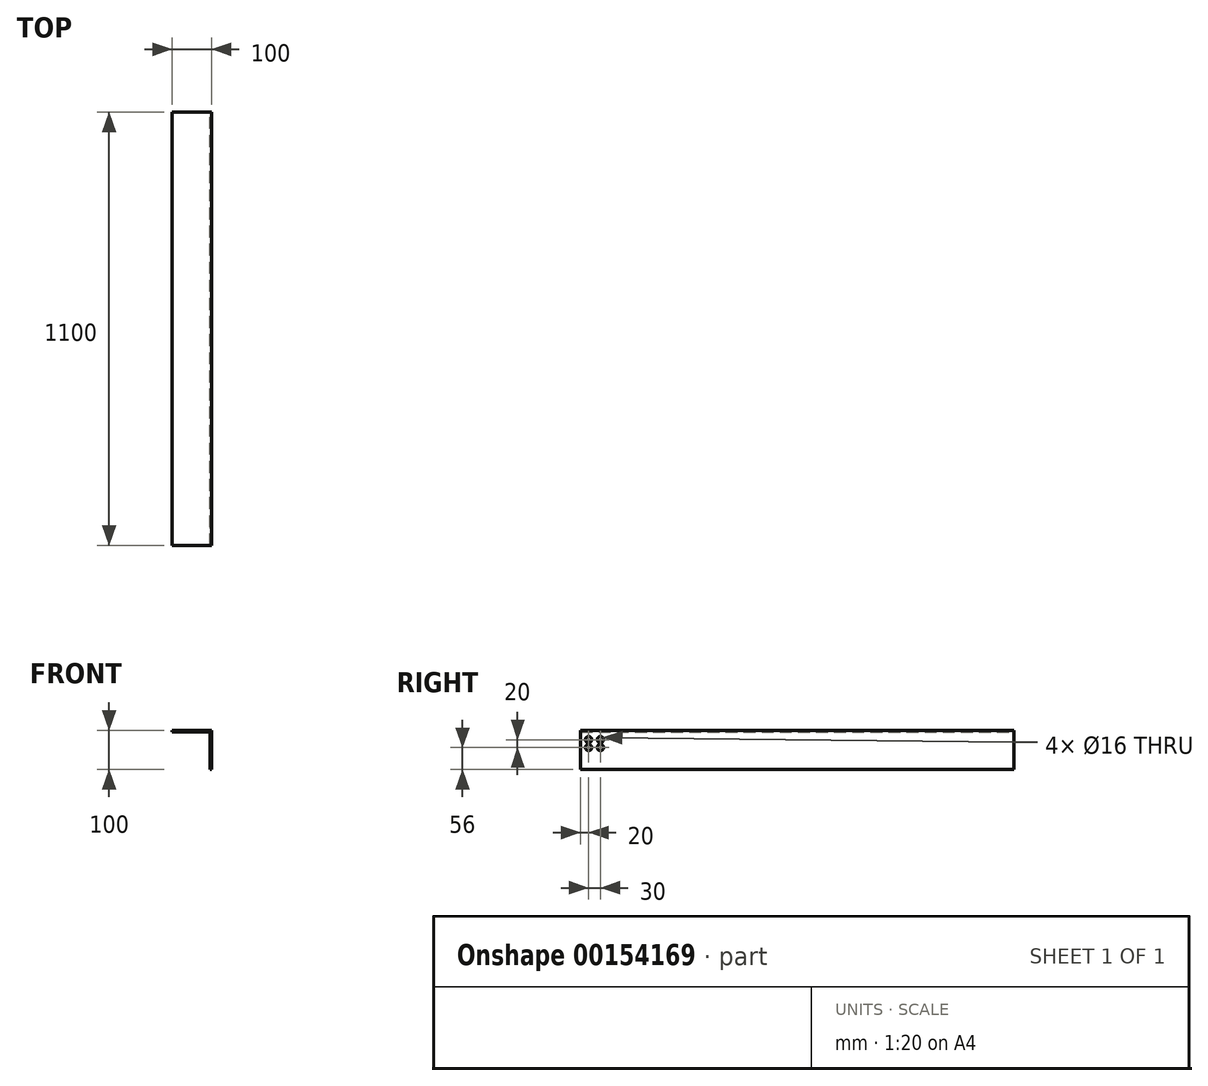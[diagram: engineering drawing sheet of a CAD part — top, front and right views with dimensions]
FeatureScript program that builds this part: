
annotation { "Feature Type Name" : "Feature", "Feature Type Description" : "" }
export const myFeature = defineFeature(function(context is Context, id is Id, definition is map)
    precondition{}
    {
        {
            var Q0;
            Q0=qCreatedBy(makeId("Front.planeOp"),FACE);
            var sketch = newSketch(context, id + "F0", { "sketchPlane" : qUnion([Q0])});
            skLineSegment(sketch, "E0", {"start": v(0, 0) * mm, "end": v(100, 0) * mm});
            skLineSegment(sketch, "E1", {"start": v(100, 0) * mm, "end": v(100, -100) * mm});
            skLineSegment(sketch, "E2", {"start": v(100, -100) * mm, "end": v(96, -100) * mm});
            skLineSegment(sketch, "E3", {"start": v(96, -100) * mm, "end": v(96, -4) * mm});
            skLineSegment(sketch, "E4", {"start": v(96, -4) * mm, "end": v(0, -4) * mm});
            skLineSegment(sketch, "E5", {"start": v(0, -4) * mm, "end": v(0, 0) * mm});
            skSolve(sketch);
        }
        {
            var Q0;
            Q0=qSketchRegion(id+"F0",true);
            extrude(context, id + "F1", {"entities" : qUnion([Q0]), "depth" : 1100 * mm});
        }
        {
            var Q0;
            Q0=makeQuery(id+"F1.opExtrude","SWEPT_FACE",FACE,{"disambiguationData":[OSD([sQuery(id+"F0.wireOp",EDGE,"E1")])]});
            var sketch = newSketch(context, id + "F2", { "sketchPlane" : qUnion([Q0])});
            skLineSegment(sketch, "E6", {"start": v(-1100, -34) * mm, "end": v(-1080, -34) * mm, "construction": true});
            skLineSegment(sketch, "E7", {"start": v(-1080, -34) * mm, "end": v(-1065, -34) * mm, "construction": true});
            skLineSegment(sketch, "E8", {"start": v(-1065, -34) * mm, "end": v(-1065, 0) * mm, "construction": true});
            skLineSegment(sketch, "E9.bottom", {"start": v(-1050, -44) * mm, "end": v(-1080, -44) * mm});
            skLineSegment(sketch, "E9.top", {"start": v(-1050, -24) * mm, "end": v(-1080, -24) * mm});
            skLineSegment(sketch, "E9.left", {"start": v(-1050, -44) * mm, "end": v(-1050, -24) * mm});
            skLineSegment(sketch, "E9.right", {"start": v(-1080, -44) * mm, "end": v(-1080, -24) * mm});
            skPoint(sketch, "E9.middle", {"position": v(-1065, -34) * mm});
            skLineSegment(sketch, "E10", {"start": v(-1050, -44) * mm, "end": v(127.39, -44) * mm, "construction": true});
            skLineSegment(sketch, "E11", {"start": v(127.39, -44) * mm, "end": v(127.39, -24) * mm, "construction": true});
            skLineSegment(sketch, "E12", {"start": v(127.39, -24) * mm, "end": v(157.39, -24) * mm, "construction": true});
            skLineSegment(sketch, "E13", {"start": v(157.39, -24) * mm, "end": v(157.39, -44) * mm, "construction": true});
            skLineSegment(sketch, "E14", {"start": v(157.39, -44) * mm, "end": v(127.39, -44) * mm, "construction": true});
            skLineSegment(sketch, "E15", {"start": v(157.39, -44) * mm, "end": v(865, -44) * mm, "construction": true});
            skLineSegment(sketch, "E16", {"start": v(865, -44) * mm, "end": v(865, -24) * mm, "construction": true});
            skLineSegment(sketch, "E17", {"start": v(865, -24) * mm, "end": v(895, -24) * mm, "construction": true});
            skLineSegment(sketch, "E18", {"start": v(895, -24) * mm, "end": v(895, -44) * mm, "construction": true});
            skLineSegment(sketch, "E19", {"start": v(895, -44) * mm, "end": v(865, -44) * mm, "construction": true});
            skLineSegment(sketch, "E20", {"start": v(895, -44) * mm, "end": v(2350, -44) * mm, "construction": true});
            skLineSegment(sketch, "E21", {"start": v(2350, -44) * mm, "end": v(2350, -24) * mm, "construction": true});
            skLineSegment(sketch, "E22", {"start": v(2350, -24) * mm, "end": v(2380, -24) * mm, "construction": true});
            skLineSegment(sketch, "E23", {"start": v(2380, -24) * mm, "end": v(2380, -44) * mm, "construction": true});
            skLineSegment(sketch, "E24", {"start": v(2380, -44) * mm, "end": v(2350, -44) * mm, "construction": true});
            skSolve(sketch);
        }
        {
            var Q0;
            Q0=sQuery(id+"F2.wireOp",VERTEX,"E9.right.end");
            var Q1;
            Q1=sQuery(id+"F2.wireOp",VERTEX,"E9.left.end");
            var Q2;
            Q2=sQuery(id+"F2.wireOp",VERTEX,"E9.right.start");
            var Q3;
            Q3=sQuery(id+"F2.wireOp",VERTEX,"E9.bottom.start");
            var Q4;
            Q4=sQuery(id+"F2.wireOp",VERTEX,"E11.start");
            var Q5;
            Q5=sQuery(id+"F2.wireOp",VERTEX,"E11.end");
            var Q6;
            Q6=sQuery(id+"F2.wireOp",VERTEX,"E12.end");
            var Q7;
            Q7=sQuery(id+"F2.wireOp",VERTEX,"E13.end");
            var Q8;
            Q8=sQuery(id+"F2.wireOp",VERTEX,"E16.start");
            var Q9;
            Q9=sQuery(id+"F2.wireOp",VERTEX,"E17.start");
            var Q10;
            Q10=sQuery(id+"F2.wireOp",VERTEX,"E17.end");
            var Q11;
            Q11=sQuery(id+"F2.wireOp",VERTEX,"E20.start");
            var Q12;
            Q12=sQuery(id+"F2.wireOp",VERTEX,"E23.start");
            var Q13;
            Q13=sQuery(id+"F2.wireOp",VERTEX,"E24.start");
            var Q14;
            Q14=sQuery(id+"F2.wireOp",VERTEX,"E21.start");
            var Q15;
            Q15=sQuery(id+"F2.wireOp",VERTEX,"E22.start");
            var Q16;
            Q16=makeQuery(id+"F1.opExtrude","SWEPT_BODY",BODY,{"disambiguationData":[OSD([sQuery(id+"F0.wireOp",EDGE,"E0"),sQuery(id+"F0.wireOp",EDGE,"E1"),sQuery(id+"F0.wireOp",EDGE,"E2"),sQuery(id+"F0.wireOp",EDGE,"E3"),sQuery(id+"F0.wireOp",EDGE,"E4"),sQuery(id+"F0.wireOp",EDGE,"E5")])]});
            hole(context, id + "F3", {"style" : HoleStyle.SIMPLE, "endStyle" : HoleEndStyle.THROUGH, "holeDiameter" : 16 * mm, "locations" : qUnion([Q0, Q1, Q2, Q3, Q4, Q5, Q6, Q7, Q8, Q9, Q10, Q11, Q12, Q13, Q14, Q15]), "scope" : qUnion([Q16]), "isTappedThrough" : true});
        }
    });
